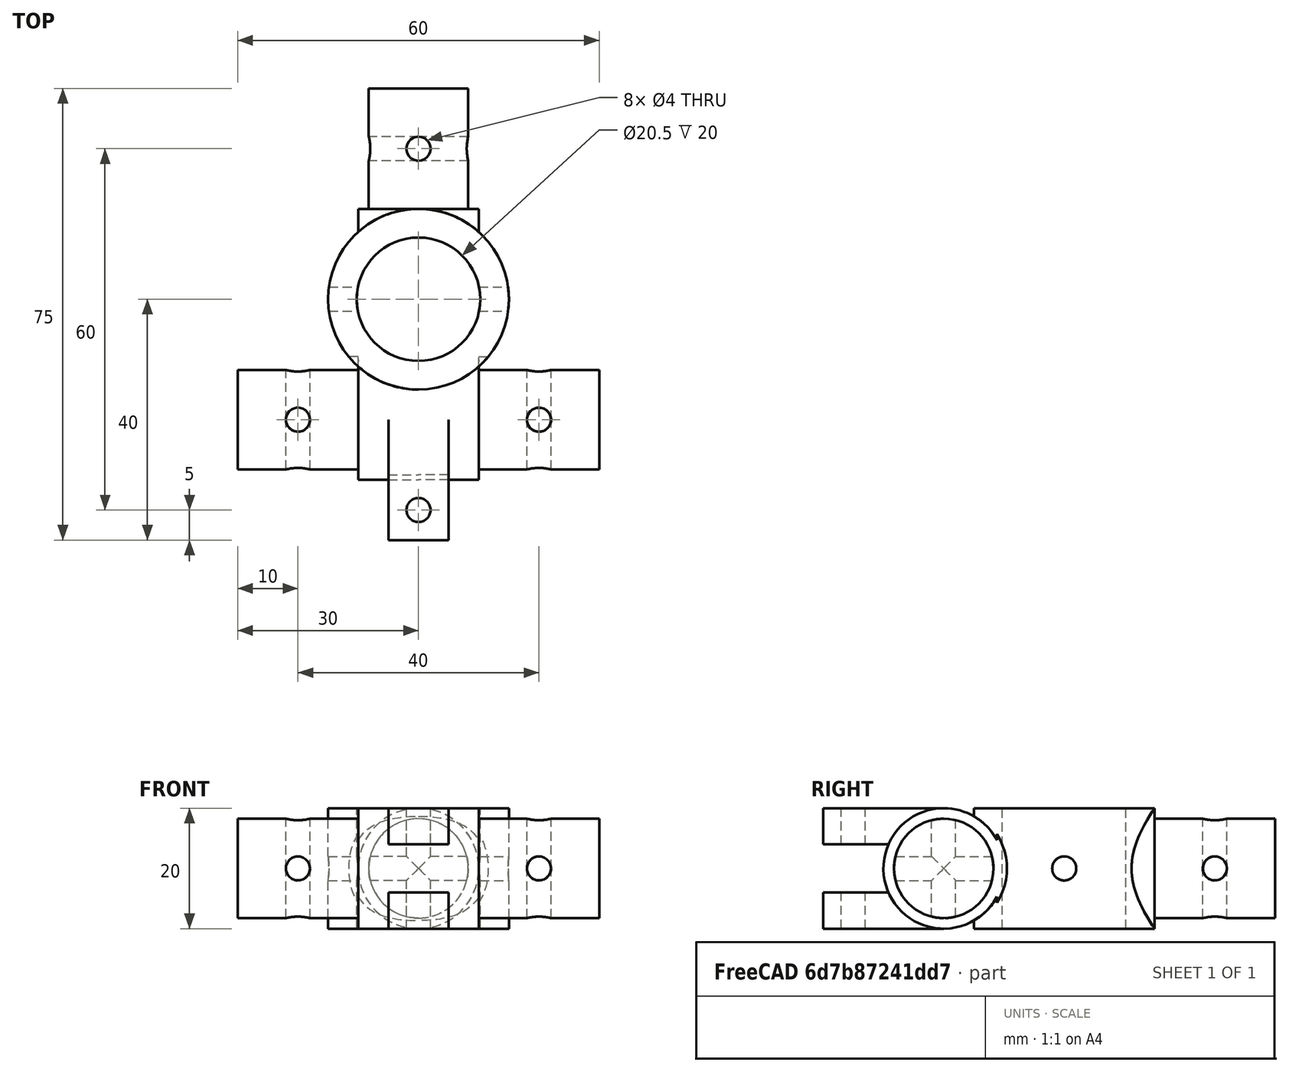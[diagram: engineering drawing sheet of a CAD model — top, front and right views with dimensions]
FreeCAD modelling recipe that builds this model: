
FCSTD DOCUMENT  (FreeCAD 0.18R16110 (Git))
Label: RailCenter
License: All rights reserved
LicenseURL: http://en.wikipedia.org/wiki/All_rights_reserved
objects: Part::Cylinder×18, Part::MultiFuse×3, Part::Cut×2, Part::Box×2
note: 25 computed .brp shape members not serialized (recipe doc carries the construction recipe); baked Part::Feature solids carry a one-line shape summary decoded from their .brp

FEATURE [Part::Cylinder] Cylinder
  Angle = 360
  AttacherType = Attacher::AttachEngine3D
  Height = 20
  Placement = pos=(0,20,-10) rot=(0,0,1;0rad)
  Radius = 15
FEATURE [Part::Cylinder] Cylinder001
  Angle = 360
  AttacherType = Attacher::AttachEngine3D
  Height = 20
  Placement = pos=(10,0,2.2e-15) rot=(0,1,0;1.5708rad)
  Radius = 8.25
FEATURE [Part::Cylinder] Cylinder002
  Angle = 360
  AttacherType = Attacher::AttachEngine3D
  Height = 10
  Placement = pos=(7e-15,35,0) rot=(0.57735,-0.57735,0.57735;2.0944rad)
  Radius = 10
FEATURE [Part::Cylinder] Cylinder003
  Angle = 360
  AttacherType = Attacher::AttachEngine3D
  Height = 20
  Placement = pos=(-10,-7e-15,-3e-15) rot=(0.707107,0,-0.707107;3.14159rad)
  Radius = 8.25
FEATURE [Part::Cylinder] Cylinder004
  Angle = 360
  AttacherType = Attacher::AttachEngine3D
  Height = 20
  Placement = pos=(-4e-15,35,0) rot=(0.57735,-0.57735,-0.57735;4.18879rad)
  Radius = 8.25
FEATURE [Part::Cylinder] Cylinder005
  Angle = 360
  AttacherType = Attacher::AttachEngine3D
  Height = 10
  Placement = pos=(10,0,4.1e-15) rot=(0,-1,0;1.5708rad)
  Radius = 10
FEATURE [Part::Cylinder] Cylinder006
  Angle = 360
  AttacherType = Attacher::AttachEngine3D
  Height = 10
  Placement = pos=(-10,-2e-15,2e-15) rot=(0.707107,0,0.707107;3.14159rad)
  Radius = 10
FEATURE [Part::Cylinder] Cylinder007
  Angle = 360
  AttacherType = Attacher::AttachEngine3D
  Height = 20
  Placement = pos=(0,20,-10) rot=(0,0,1;0rad)
  Radius = 10.25
FEATURE [Part::Cylinder] Cylinder009
  Angle = 360
  AttacherType = Attacher::AttachEngine3D
  Height = 20
  Placement = pos=(-20,-10,2.2e-15) rot=(1,0,0;4.71239rad)
  Radius = 2
FEATURE [Part::Cylinder] Cylinder010
  Angle = 360
  AttacherType = Attacher::AttachEngine3D
  Height = 20
  Placement = pos=(0,45,-10) rot=(0,0,1;0rad)
  Radius = 2
FEATURE [Part::Cylinder] Cylinder011
  Angle = 360
  AttacherType = Attacher::AttachEngine3D
  Height = 20
  Placement = pos=(20,0,-10) rot=(0,0,1;0rad)
  Radius = 2
FEATURE [Part::Cylinder] Cylinder012
  Angle = 360
  AttacherType = Attacher::AttachEngine3D
  Height = 20
  Placement = pos=(-20,0,-10) rot=(0,0,1;0rad)
  Radius = 2
FEATURE [Part::Cylinder] Cylinder013
  Angle = 360
  AttacherType = Attacher::AttachEngine3D
  Height = 20
  Placement = pos=(20,-10,2e-15) rot=(-1,0,0;1.5708rad)
  Radius = 2
FEATURE [Part::Cylinder] Cylinder014
  Angle = 360
  AttacherType = Attacher::AttachEngine3D
  Height = 20
  Placement = pos=(10,45,9.8e-15) rot=(0.57735,0.57735,-0.57735;4.18879rad)
  Radius = 2
FEATURE [Part::Cylinder] Cylinder015
  Angle = 360
  AttacherType = Attacher::AttachEngine3D
  Height = 30
  Placement = pos=(-15,20,8.7e-15) rot=(-0.57735,0.57735,-0.57735;2.0944rad)
  Radius = 2
FEATURE [Part::Cylinder] Cylinder016
  Angle = 360
  AttacherType = Attacher::AttachEngine3D
  Height = 10
  Placement = pos=(10,0,2.6e-15) rot=(0,1,0;1.5708rad)
  Radius = 10.5
FEATURE [Part::Cylinder] Cylinder017
  Angle = 360
  AttacherType = Attacher::AttachEngine3D
  Height = 10
  Placement = pos=(-10,0,-1.4e-15) rot=(0,1,0;4.71239rad)
  Radius = 10.5
FEATURE [Part::MultiFuse] Fusion002
  Shapes = -> [Cylinder016,Cylinder017]
FEATURE [Part::Cut] Cut001
  Base = -> Cylinder
  Tool = -> Fusion002
FEATURE [Part::Box] Box001  label="Cube001"
  AttacherType = Attacher::AttachEngine3D
  Height = 6
  Length = 10
  Placement = pos=(-5,-20,-10) rot=(0,0,1;0rad)
  Width = 20
FEATURE [Part::Box] Box002  label="Cube002"
  AttacherType = Attacher::AttachEngine3D
  Height = 6
  Length = 10
  Placement = pos=(-5,-20,4) rot=(0,0,1;0rad)
  Width = 20
FEATURE [Part::MultiFuse] Fusion  label="Positive Fusion"
  Shapes = -> [Cylinder001,Cylinder002,Cylinder003,Cylinder004,Cylinder006,Cylinder005,Cut001,Box001,Box002]
FEATURE [Part::Cylinder] Cylinder018
  Angle = 360
  AttacherType = Attacher::AttachEngine3D
  Height = 20
  Placement = pos=(0,-15,-10) rot=(0,0,1;0rad)
  Radius = 2
FEATURE [Part::MultiFuse] Fusion001  label="Negative Fusion"
  Shapes = -> [Cylinder007,Cylinder009,Cylinder010,Cylinder011,Cylinder012,Cylinder013,Cylinder014,Cylinder015,Cylinder018]
FEATURE [Part::Cut] Cut
  Base = -> Fusion
  Tool = -> Fusion001
